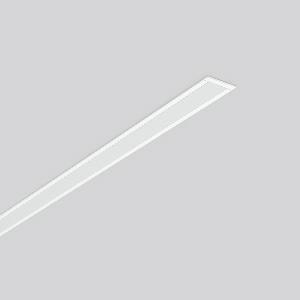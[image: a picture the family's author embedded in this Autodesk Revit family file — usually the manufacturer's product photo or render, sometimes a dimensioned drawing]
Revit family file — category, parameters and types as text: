
# Revit family: less_is_more_27_312178_002_1_76_c11b
name_source: partatom
category: Lighting Fixtures
units: mm (PartAtom-declared; Revit-internal decimal feet)

## family parameters
Cut with Voids When Loaded = No
Host = Face
Light Source = No
Part Type = Normal
Room Calculation Point = No
Round Connector Dimension = Use Diameter
Shared = No

## types (1)
- LESS IS MORE 27 (1 x LED Modul 840, 2900 lm, 4000)
    Apparent Load = 39 VA
    CIE Flux Codes = 48 79 96 100 100
    Color Rendering = 80
    Color Temperature = 4000
    Default Elevation = 1800 mm
    Description = Series: LESS IS MORE 27
Recessed ceiling and wall luminaire with slim design. Housing: extruded aluminium profile, powder-coated. End cap aluminium powder-coated. Diffuser made of non-yellowing plastic (PMMA), opal. Suitable for Recessed ceiling mounting, wall (recessed). External driver with connecting cable. 
Colour: traffic white, matt (RAL 9016)
Length: 1514 mm
Width: 38 mm
Height: 2 mm
Cut-out length: 1506 mm
Cut-out width: 30 mm
Recess height: 45-60 mm
Luminaire: recess height: 37 mm
Lamp: LED
Socket: without socket
Colour temperature: 4000K
Colour rendering index (CRI): 82
System power: 39 W
Rated luminous flux: 2900 lm
Luminous efficiency: 74 lm/W
Control gear: Voltage converter, DALI dim.
Protection class: II
Type of protection: IP 20
    Height = 0 mm  [stored 0 ft]
    Lamp = 1 x LED Modul 840
    Lamp Light Flux = 2900 lm
    Lamp count = 1
    Length = 1514 mm
    Lifetime = 50000 h
    Luminous efficacy = 74 lm/W
    Manufacturer = RZB
    ModVariant = No
    Model = 312178.002.1.76
    Mounting Place = Ceiling, Wall
    Mounting Type = Recessed
    Number of Poles = 1
    OnlyDefault = Yes
    Power Factor = 1
    Product Name = LESS IS MORE 27
    Product group = Recessed LED linear luminaires
    ProductGroupID = 407
    Protection Class = Protection class II
    Protection Degree = IP 20
    RLX_Detail_Level = 1
    RLX_Emergency_Light_Flux = 0 lm
    RLX_Emergency_Type = 0
    RLX_Emergency_Type_DB = No
    RlxData = <blob elided: 21589 chars, md5=759fd9ac>
    Socket = socket
    Standby Power = 0 W
    System Light Flux = 2900 lm
    System Power = 39 W
    Type Comments = Product without accessories
    Type Image = 312176.002.jpg
    URL = http://relux.com
    VarID = ---
    Voltage = 230 V
    Voltage Range = 220-240 V
    Weight = 0.00 kg
    Width = 38 mm

note: [stored X ft] marks values corroborated as IEEE doubles in the binary element streams (Revit-internal decimal feet)

## geometry (parser evidence)
native form markers: Blend x4, Sweep x12
no freeform markers — native parametric forms only
